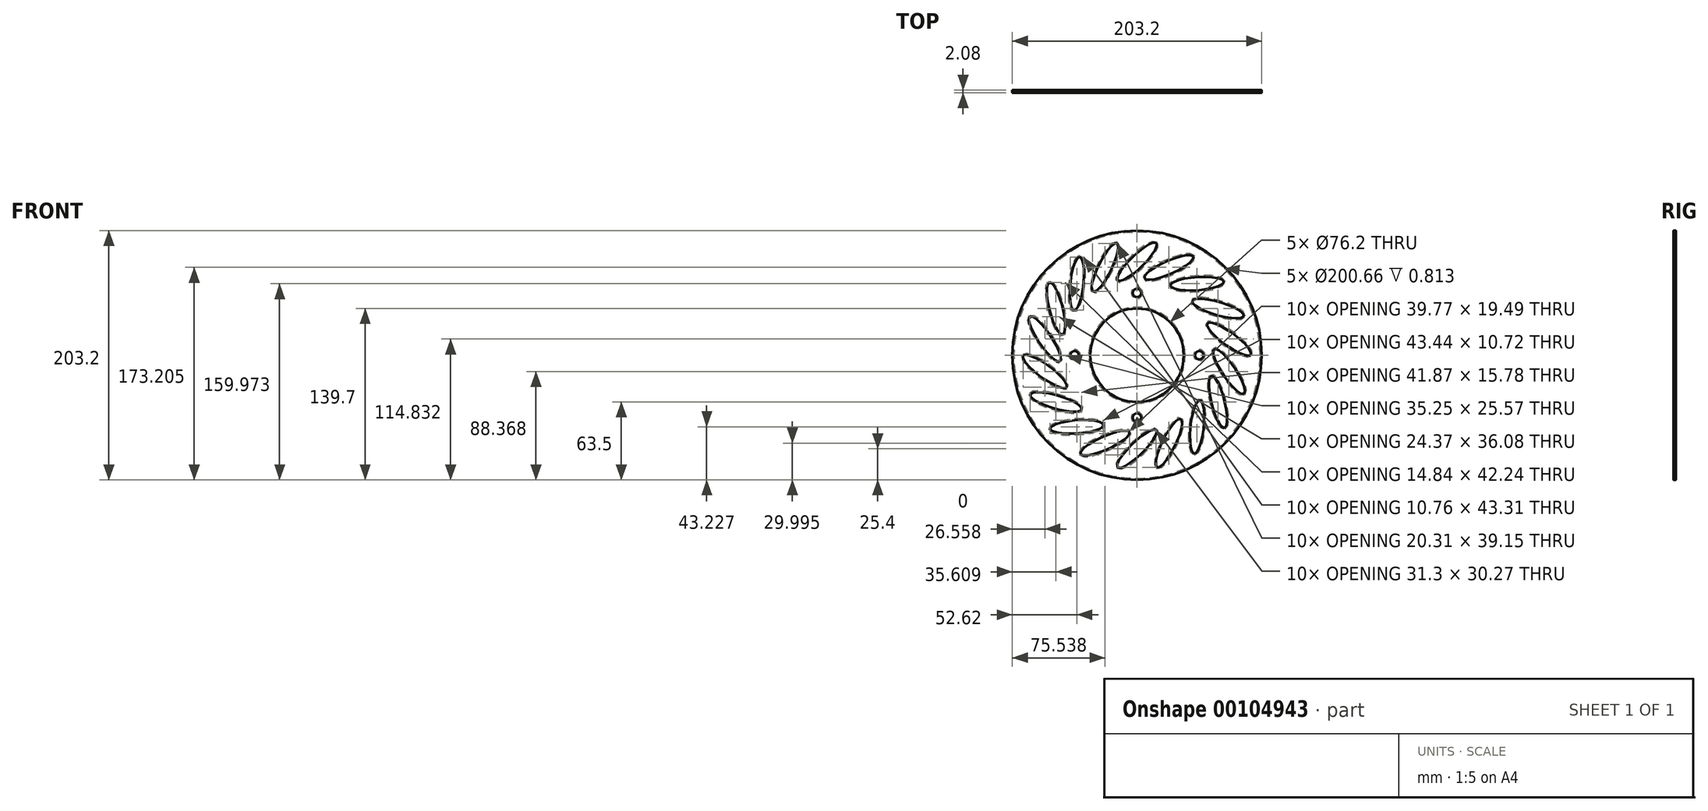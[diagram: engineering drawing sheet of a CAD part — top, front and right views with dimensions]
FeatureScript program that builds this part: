
annotation { "Feature Type Name" : "Feature", "Feature Type Description" : "" }
export const myFeature = defineFeature(function(context is Context, id is Id, definition is map)
    precondition{}
    {
        {
            var Q0;
            Q0=qCreatedBy(makeId("Front.planeOp"),FACE);
            var sketch = newSketch(context, id + "F0", { "sketchPlane" : qUnion([Q0])});
            skCircle(sketch, "E0", {"center": v(0, 0) * mm, "radius": 38.1 * mm});
            skCircle(sketch, "E1", {"center": v(0, 0) * mm, "radius": 101.6 * mm});
            skCircle(sketch, "E2", {"center": v(0, 50.8) * mm, "radius": 3.4 * mm});
            skCircle(sketch, "E3", {"center": v(-50.8, 0) * mm, "radius": 3.4 * mm});
            skCircle(sketch, "E4", {"center": v(0, -50.8) * mm, "radius": 3.4 * mm});
            skCircle(sketch, "E5", {"center": v(50.8, 0) * mm, "radius": 3.4 * mm});
            skEllipse(sketch, "E6", {"center": v(0, 76.2) * mm, "majorRadius": 21.77 * mm, "minorRadius": 5.38 * mm, "majorAxis": v(-0.72, -0.7)});
            skEllipse(sketch, "E7.1.0", {"center": v(-26.06, 71.6) * mm, "majorRadius": 21.77 * mm, "minorRadius": 5.38 * mm, "majorAxis": v(-0.44, -0.9)});
            skEllipse(sketch, "E7.2.0", {"center": v(-48.98, 58.37) * mm, "majorRadius": 21.77 * mm, "minorRadius": 5.38 * mm, "majorAxis": v(-0.1, -1)});
            skEllipse(sketch, "E7.3.0", {"center": v(-66, 38.1) * mm, "majorRadius": 21.77 * mm, "minorRadius": 5.38 * mm, "majorAxis": v(0.24, -0.97)});
            skEllipse(sketch, "E7.4.0", {"center": v(-75.04, 13.23) * mm, "majorRadius": 21.77 * mm, "minorRadius": 5.38 * mm, "majorAxis": v(0.56, -0.83)});
            skEllipse(sketch, "E7.5.0", {"center": v(-75.04, -13.23) * mm, "majorRadius": 21.77 * mm, "minorRadius": 5.38 * mm, "majorAxis": v(0.8, -0.59)});
            skEllipse(sketch, "E7.6.0", {"center": v(-66, -38.1) * mm, "majorRadius": 21.77 * mm, "minorRadius": 5.38 * mm, "majorAxis": v(0.96, -0.27)});
            skEllipse(sketch, "E7.7.0", {"center": v(-48.98, -58.37) * mm, "majorRadius": 21.77 * mm, "minorRadius": 5.38 * mm, "majorAxis": v(1, 0.07)});
            skEllipse(sketch, "E7.8.0", {"center": v(-26.06, -71.6) * mm, "majorRadius": 21.77 * mm, "minorRadius": 5.38 * mm, "majorAxis": v(0.91, 0.4)});
            skEllipse(sketch, "E7.9.0", {"center": v(0, -76.2) * mm, "majorRadius": 21.77 * mm, "minorRadius": 5.38 * mm, "majorAxis": v(0.72, 0.7)});
            skEllipse(sketch, "E7.10.0", {"center": v(26.06, -71.6) * mm, "majorRadius": 21.77 * mm, "minorRadius": 5.38 * mm, "majorAxis": v(0.44, 0.9)});
            skEllipse(sketch, "E7.11.0", {"center": v(48.98, -58.37) * mm, "majorRadius": 21.77 * mm, "minorRadius": 5.38 * mm, "majorAxis": v(0.1, 1)});
            skEllipse(sketch, "E7.12.0", {"center": v(66, -38.1) * mm, "majorRadius": 21.77 * mm, "minorRadius": 5.38 * mm, "majorAxis": v(-0.24, 0.97)});
            skEllipse(sketch, "E7.13.0", {"center": v(75.04, -13.23) * mm, "majorRadius": 21.77 * mm, "minorRadius": 5.38 * mm, "majorAxis": v(-0.56, 0.83)});
            skEllipse(sketch, "E7.14.0", {"center": v(75.04, 13.23) * mm, "majorRadius": 21.77 * mm, "minorRadius": 5.38 * mm, "majorAxis": v(-0.8, 0.59)});
            skEllipse(sketch, "E7.15.0", {"center": v(66, 38.1) * mm, "majorRadius": 21.77 * mm, "minorRadius": 5.38 * mm, "majorAxis": v(-0.96, 0.27)});
            skEllipse(sketch, "E7.16.0", {"center": v(48.98, 58.37) * mm, "majorRadius": 21.77 * mm, "minorRadius": 5.38 * mm, "majorAxis": v(-1, -0.07)});
            skEllipse(sketch, "E7.17.0", {"center": v(26.06, 71.6) * mm, "majorRadius": 21.77 * mm, "minorRadius": 5.38 * mm, "majorAxis": v(-0.91, -0.4)});
            skSolve(sketch);
        }
        {
            var Q0;
            Q0 = qSketchRegion(id + "F0", true);
            extrude(context, id + "F1", {"entities" : qUnion([Q0]), "depth" : 2.08 * mm});
        }
        {
            var Q0;
            Q0=makeQuery(id+"F1.opExtrude","CAP_EDGE",EDGE,{"disambiguationData":[OSD([sQuery(id+"F0.wireOp",EDGE,"E1")])],"isStart":false});
            var Q1;
            Q1=makeQuery(id+"F1.opExtrude","CAP_EDGE",EDGE,{"disambiguationData":[OSD([sQuery(id+"F0.wireOp",EDGE,"E1")])],"isStart":true});
            var Q2;
            Q2=makeQuery(id+"F1.opExtrude","CAP_EDGE",EDGE,{"disambiguationData":[OSD([sQuery(id+"F0.wireOp",EDGE,"E0")])],"isStart":false});
            var Q3;
            Q3=makeQuery(id+"F1.opExtrude","CAP_EDGE",EDGE,{"disambiguationData":[OSD([sQuery(id+"F0.wireOp",EDGE,"E0")])],"isStart":true});
            fillet(context, id + "F2", {"entities" : qUnion([Q0, Q1, Q2, Q3]), "radius" : 0.25 * mm, "tangentPropagation" : true, "allowEdgeOverflow" : false});
        }
        {
            var Q0;
            Q0=makeQuery(id+"F1.opExtrude","CAP_FACE",FACE,{"disambiguationData":[OSD([sQuery(id+"F0.wireOp",EDGE,"E0"),sQuery(id+"F0.wireOp",EDGE,"E1"),sQuery(id+"F0.wireOp",EDGE,"E2"),sQuery(id+"F0.wireOp",EDGE,"E3"),sQuery(id+"F0.wireOp",EDGE,"E4"),sQuery(id+"F0.wireOp",EDGE,"E5"),sQuery(id+"F0.wireOp",EDGE,"E6"),sQuery(id+"F0.wireOp",EDGE,"E7.1.0"),sQuery(id+"F0.wireOp",EDGE,"E7.2.0"),sQuery(id+"F0.wireOp",EDGE,"E7.3.0"),sQuery(id+"F0.wireOp",EDGE,"E7.4.0"),sQuery(id+"F0.wireOp",EDGE,"E7.5.0"),sQuery(id+"F0.wireOp",EDGE,"E7.6.0"),sQuery(id+"F0.wireOp",EDGE,"E7.7.0"),sQuery(id+"F0.wireOp",EDGE,"E7.8.0"),sQuery(id+"F0.wireOp",EDGE,"E7.9.0"),sQuery(id+"F0.wireOp",EDGE,"E7.10.0"),sQuery(id+"F0.wireOp",EDGE,"E7.11.0"),sQuery(id+"F0.wireOp",EDGE,"E7.12.0"),sQuery(id+"F0.wireOp",EDGE,"E7.13.0"),sQuery(id+"F0.wireOp",EDGE,"E7.14.0"),sQuery(id+"F0.wireOp",EDGE,"E7.15.0"),sQuery(id+"F0.wireOp",EDGE,"E7.16.0"),sQuery(id+"F0.wireOp",EDGE,"E7.17.0")])],"isStart":true});
            shell(context, id + "F3", {"entities" : qUnion([Q0]), "thickness" : 1.27 * mm});
        }
    });
